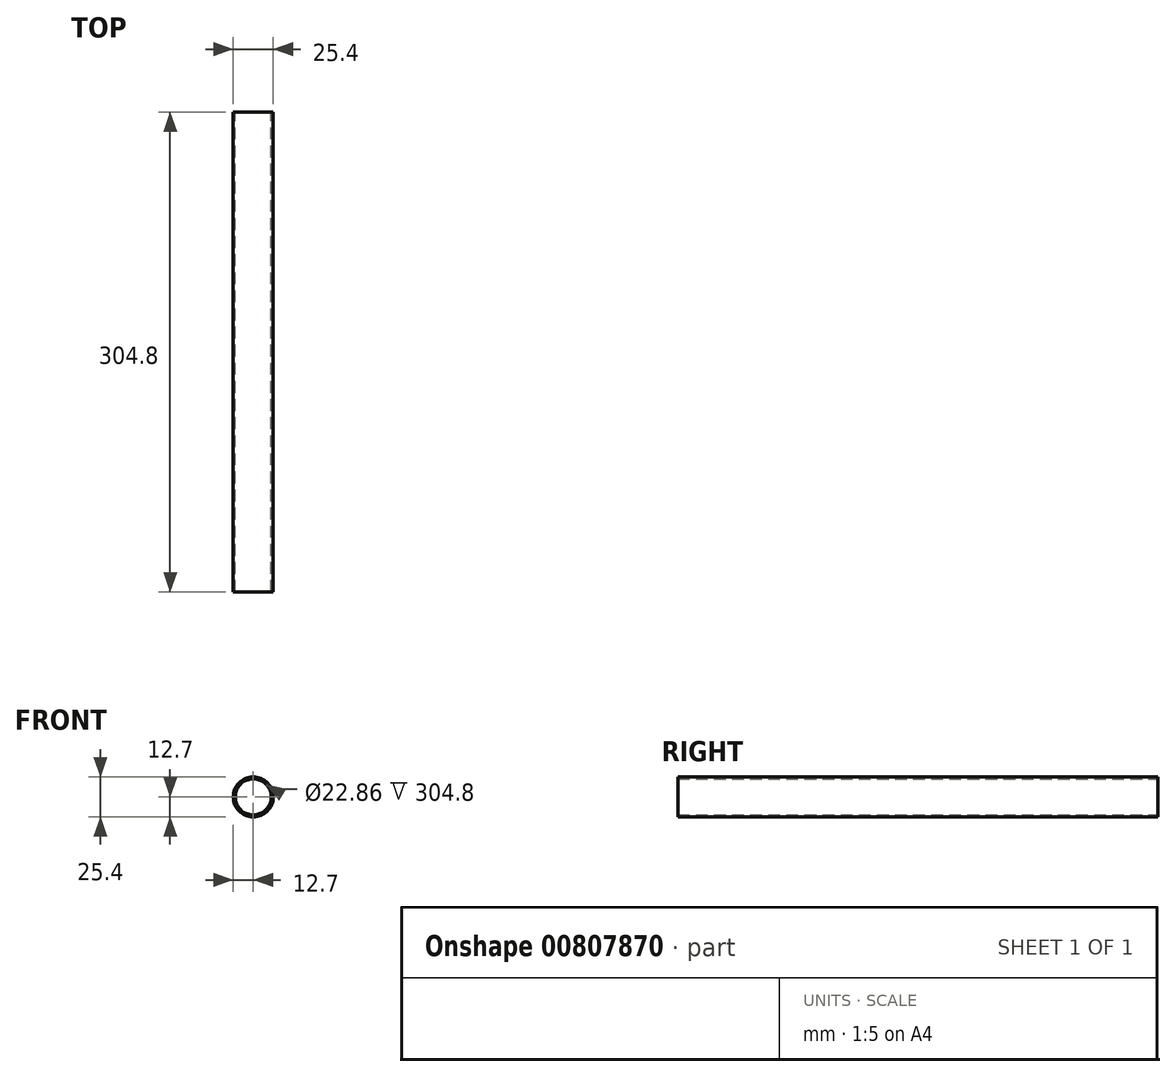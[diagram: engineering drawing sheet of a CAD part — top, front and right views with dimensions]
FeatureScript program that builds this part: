
annotation { "Feature Type Name" : "Feature", "Feature Type Description" : "" }
export const myFeature = defineFeature(function(context is Context, id is Id, definition is map)
    precondition{}
    {
        {
            var Q0;
            Q0=qCreatedBy(makeId("Front.planeOp"),FACE);
            var sketch = newSketch(context, id + "F0", { "sketchPlane" : qUnion([Q0])});
            skCircle(sketch, "E0", {"center": v(0, 12.7) * mm, "radius": 12.7 * mm});
            skCircle(sketch, "E1", {"center": v(0, 12.7) * mm, "radius": 11.43 * mm});
            skSolve(sketch);
        }
        {
            var Q0;
            Q0=makeQuery(id+"F0.imprint","IMPRINT",FACE,{"disambiguationData":[TD([[makeQuery(id+"F0.imprint","IMPRINT",EDGE,{"derivedFrom":sQuery(id+"F0.wireOp",EDGE,"E0")}),1.0]])]});
            extrude(context, id + "F1", {"entities" : qUnion([Q0]), "endBound" : BoundingType.SYMMETRIC, "depth" : 304.8 * mm, "offsetDistance" : 25.4 * mm});
        }
    });
